FCSTD DOCUMENT  (FreeCAD 0.19R24276 (Git))
Label: Knif_master_sketch
License: All rights reserved
LicenseURL: http://en.wikipedia.org/wiki/All_rights_reserved
objects: Sketcher::SketchObject×1, PartDesign::Body×1
note: 2 computed .brp shape members not serialized (recipe doc carries the construction recipe); baked Part::Feature solids carry a one-line shape summary decoded from their .brp

FEATURE [Sketcher::SketchObject] Sketch
  FullyConstrained = false
  MapMode = 5
  Support = -> [XY_Plane]
  sketch-geometry (16):
    g0: Circle CenterX=0 CenterY=0 CenterZ=0 NormalX=0 NormalY=0 NormalZ=1 AngleXU=0 Radius=44.5
    g1: LineSegment StartX=0 StartY=0 StartZ=0 EndX=-17.6802 EndY=40.837 EndZ=0
    g2: LineSegment StartX=-17.6802 StartY=40.837 StartZ=0 EndX=-97.6802 EndY=48.8773 EndZ=0
    g3: Circle CenterX=149.248 CenterY=-15 CenterZ=0 NormalX=0 NormalY=0 NormalZ=1 AngleXU=0 Radius=44.5
    g4: LineSegment StartX=149.248 StartY=-15 StartZ=0 EndX=131.568 EndY=25.837 EndZ=0
    g5: LineSegment StartX=131.568 StartY=25.837 StartZ=0 EndX=-17.6802 EndY=40.837 EndZ=0
    g6: Circle CenterX=-80 CenterY=0 CenterZ=0 NormalX=0 NormalY=0 NormalZ=1 AngleXU=0 Radius=44.5
    g7: LineSegment StartX=149.248 StartY=-15 StartZ=0 EndX=0 EndY=0 EndZ=0
    g8: LineSegment StartX=0 StartY=0 StartZ=0 EndX=-120.957 EndY=12.1567 EndZ=0
    g9: Circle CenterX=-80 CenterY=8.0403 CenterZ=0 NormalX=0 NormalY=0 NormalZ=1 AngleXU=0 Radius=44.5
    g10: Circle CenterX=0 CenterY=0 CenterZ=0 NormalX=0 NormalY=0 NormalZ=1 AngleXU=0 Radius=22.5
    g11: Circle CenterX=149.248 CenterY=-15 CenterZ=0 NormalX=0 NormalY=0 NormalZ=1 AngleXU=0 Radius=22.5
    g12: LineSegment StartX=0 StartY=0 StartZ=0 EndX=-22.2745 EndY=3.17762 EndZ=0
    g13: LineSegment StartX=149.248 StartY=-15 StartZ=0 EndX=135.988 EndY=3.17762 EndZ=0
    g14: LineSegment StartX=135.988 StartY=3.17762 StartZ=0 EndX=-22.2745 EndY=3.17762 EndZ=0
    g15: LineSegment StartX=-22.2745 StartY=3.17762 StartZ=0 EndX=-122.274 EndY=3.17762 EndZ=0
  constraints (39):
    c: Coincident(g0,g-1)
    c: Diameter(g0) = 89
    c: Coincident(g1,g0)
    c: PointOnObject(g1,g0)
    c: Coincident(g2,g1)
    c: DistanceX(g2,g2) = 80
    c: Coincident(g4,g3)
    c: PointOnObject(g4,g3)
    c: Coincident(g5,g4)
    c: Coincident(g5,g1)
    c: Distance(g5) = 150
    c: Distance(g0,g3) = 150
    c: DistanceY(g3,g0) = 15
    c: Parallel(g2,g5)
    c: Equal(g0,g3)
    c: Equal(g6,g0)
    c: DistanceX(g6,g0) = 80
    c: DistanceY(g6,g0) = 0
    c: Coincident(g7,g3)
    c: Coincident(g7,g0)
    c: Coincident(g8,g0)
    c: Parallel(g8,g7)
    c: PointOnObject(g9,g8)
    c: Equal(g6,g9)
    c: DistanceX(g9,g0) = 80
    c: Coincident(g10,g0)
    c: Coincident(g11,g3)
    c: Equal(g10,g11)
    c: Diameter(g10) = 45
    c: Coincident(g12,g0)
    c: Coincident(g13,g3)
    c: PointOnObject(g13,g11)
    c: PointOnObject(g12,g10)
    c: Coincident(g14,g13)
    c: Coincident(g14,g12)
    c: Horizontal(g14)
    c: Coincident(g15,g12)
    c: Parallel(g15,g14)
    c: DistanceX(g15,g12) = 100
FEATURE [PartDesign::Body] Body
  Group = -> [Sketch]
  Origin = -> Origin
